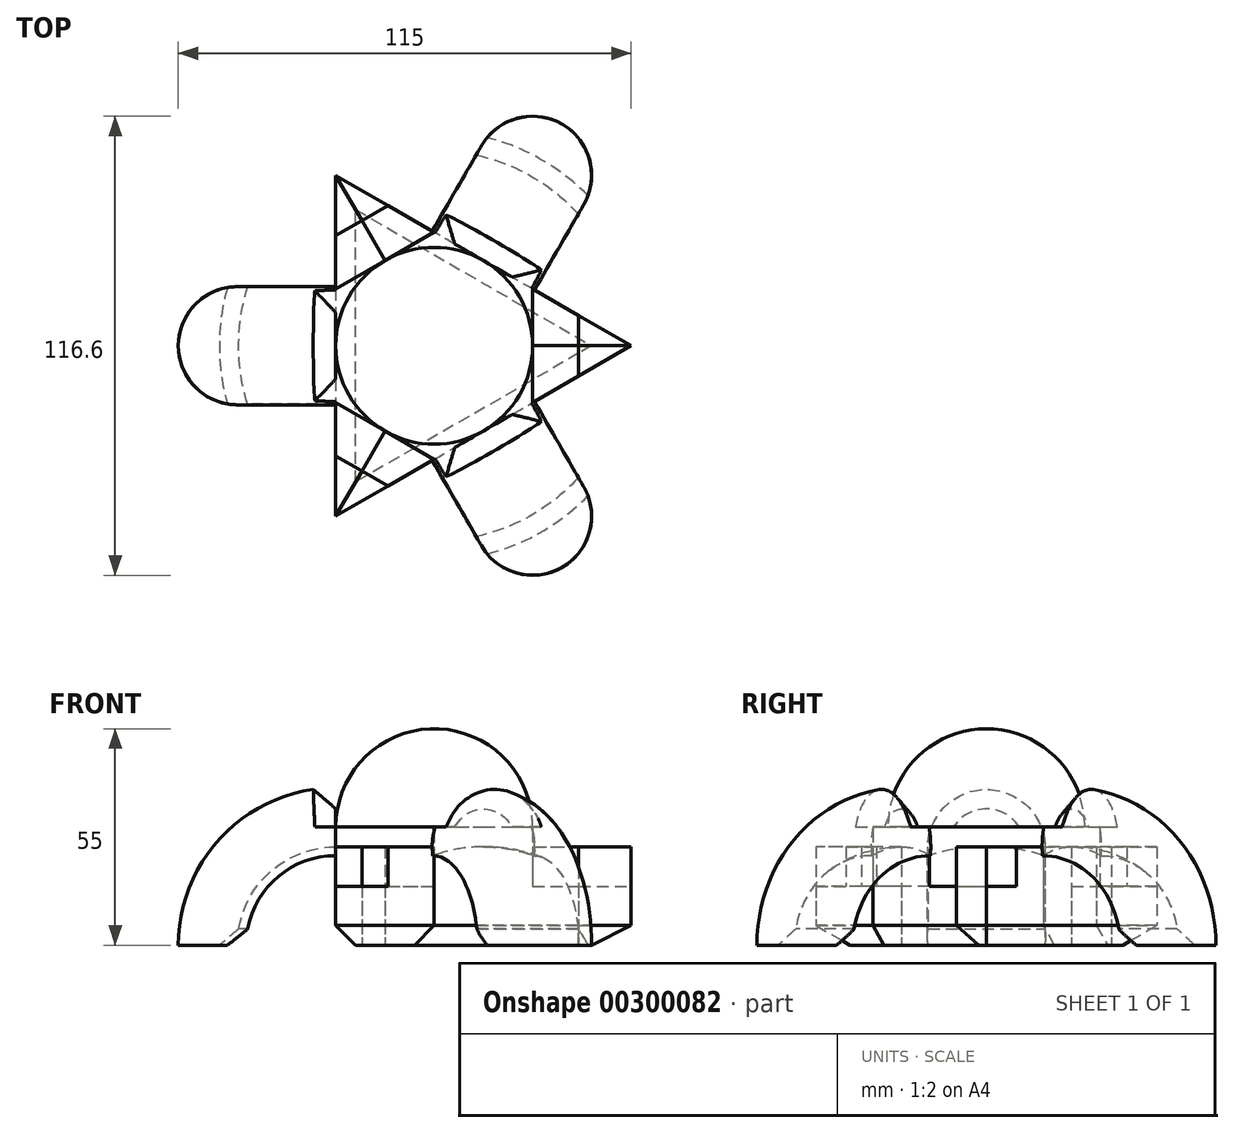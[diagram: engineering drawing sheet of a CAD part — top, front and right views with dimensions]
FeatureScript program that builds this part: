
annotation { "Feature Type Name" : "Feature", "Feature Type Description" : "" }
export const myFeature = defineFeature(function(context is Context, id is Id, definition is map)
    precondition{}
    {
        {
            var Q0;
            Q0=qCreatedBy(makeId("Top.planeOp"),FACE);
            var sketch = newSketch(context, id + "F0", { "sketchPlane" : qUnion([Q0])});
            skCircle(sketch, "E0", {"center": v(0, 0) * mm, "radius": 50 * mm});
            skCircle(sketch, "E1", {"center": v(-50, 0) * mm, "radius": 15 * mm});
            skCircle(sketch, "E2.1.0", {"center": v(25, -43.3) * mm, "radius": 15 * mm});
            skCircle(sketch, "E2.2.0", {"center": v(25, 43.3) * mm, "radius": 15 * mm});
            skLineSegment(sketch, "E3", {"start": v(-50, 0) * mm, "end": v(25, 43.3) * mm});
            skLineSegment(sketch, "E4", {"start": v(25, -43.3) * mm, "end": v(25, 43.3) * mm});
            skLineSegment(sketch, "E5", {"start": v(-50, 0) * mm, "end": v(25, -43.3) * mm});
            skLineSegment(sketch, "E6", {"start": v(25, 43.3) * mm, "end": v(-25, -43.3) * mm});
            skLineSegment(sketch, "E7", {"start": v(25, -43.3) * mm, "end": v(-25, 43.3) * mm});
            skLineSegment(sketch, "E8", {"start": v(-50, 0) * mm, "end": v(50, 0) * mm});
            skLineSegment(sketch, "E9", {"start": v(-25, 43.3) * mm, "end": v(-25, -43.3) * mm});
            skLineSegment(sketch, "E10", {"start": v(-25, 43.3) * mm, "end": v(50, 0) * mm});
            skLineSegment(sketch, "E11", {"start": v(-25, -43.3) * mm, "end": v(50, 0) * mm});
            skLineSegment(sketch, "E12", {"start": v(-47.75, -14.83) * mm, "end": v(11.03, -48.77) * mm});
            skLineSegment(sketch, "E13", {"start": v(36.72, -33.94) * mm, "end": v(36.72, 33.94) * mm});
            skLineSegment(sketch, "E14", {"start": v(11.03, 48.77) * mm, "end": v(-47.75, 14.83) * mm});
            skLineSegment(sketch, "E15", {"start": v(11.03, 48.77) * mm, "end": v(36.72, 33.94) * mm});
            skLineSegment(sketch, "E16", {"start": v(36.72, -33.94) * mm, "end": v(11.03, -48.77) * mm});
            skLineSegment(sketch, "E17", {"start": v(-47.75, -14.83) * mm, "end": v(-47.75, 14.83) * mm});
            skSolve(sketch);
        }
        {
            var Q0;
            {var subQ0=sQuery(id+"F0.wireOp",EDGE,"E11");var subQ1=sQuery(id+"F0.wireOp",EDGE,"E4");var subQ2=makeQuery(id+"F0.imprint","INTERSECT",VERTEX,{"derivedFrom":[subQ1,subQ0]});Q0=makeQuery(id+"F0.imprint","IMPRINT",FACE,{"disambiguationData":[TD([[makeQuery(id+"F0.imprint","IMPRINT",EDGE,{"disambiguationData":[TD([[subQ2,-1.0]])],"derivedFrom":subQ1}),1.0]])]});}
            var Q1;
            {var subQ0=sQuery(id+"F0.wireOp",EDGE,"E8");var subQ1=sQuery(id+"F0.wireOp",EDGE,"E4");var subQ2=makeQuery(id+"F0.imprint","INTERSECT",VERTEX,{"derivedFrom":[subQ1,subQ0]});Q1=makeQuery(id+"F0.imprint","IMPRINT",FACE,{"disambiguationData":[TD([[makeQuery(id+"F0.imprint","IMPRINT",EDGE,{"disambiguationData":[TD([[subQ2,-1.0]])],"derivedFrom":subQ1}),1.0]])]});}
            var Q2;
            {var subQ0=sQuery(id+"F0.wireOp",EDGE,"E7");var subQ1=sQuery(id+"F0.wireOp",EDGE,"E3");var subQ2=makeQuery(id+"F0.imprint","INTERSECT",VERTEX,{"derivedFrom":[subQ1,subQ0]});Q2=makeQuery(id+"F0.imprint","IMPRINT",FACE,{"disambiguationData":[TD([[makeQuery(id+"F0.imprint","IMPRINT",EDGE,{"disambiguationData":[TD([[subQ2,-1.0]])],"derivedFrom":subQ1}),-1.0]])]});}
            var Q3;
            {var subQ0=sQuery(id+"F0.wireOp",EDGE,"E9");var subQ1=sQuery(id+"F0.wireOp",EDGE,"E3");var subQ2=makeQuery(id+"F0.imprint","INTERSECT",VERTEX,{"derivedFrom":[subQ1,subQ0]});Q3=makeQuery(id+"F0.imprint","IMPRINT",FACE,{"disambiguationData":[TD([[makeQuery(id+"F0.imprint","IMPRINT",EDGE,{"disambiguationData":[TD([[subQ2,-1.0]])],"derivedFrom":subQ1}),-1.0]])]});}
            var Q4;
            {var subQ0=sQuery(id+"F0.wireOp",EDGE,"E9");var subQ1=sQuery(id+"F0.wireOp",EDGE,"E5");var subQ2=makeQuery(id+"F0.imprint","INTERSECT",VERTEX,{"derivedFrom":[subQ1,subQ0]});Q4=makeQuery(id+"F0.imprint","IMPRINT",FACE,{"disambiguationData":[TD([[makeQuery(id+"F0.imprint","IMPRINT",EDGE,{"disambiguationData":[TD([[subQ2,-1.0]])],"derivedFrom":subQ1}),1.0]])]});}
            var Q5;
            {var subQ0=sQuery(id+"F0.wireOp",EDGE,"E6");var subQ1=sQuery(id+"F0.wireOp",EDGE,"E5");var subQ2=makeQuery(id+"F0.imprint","INTERSECT",VERTEX,{"derivedFrom":[subQ1,subQ0]});Q5=makeQuery(id+"F0.imprint","IMPRINT",FACE,{"disambiguationData":[TD([[makeQuery(id+"F0.imprint","IMPRINT",EDGE,{"disambiguationData":[TD([[subQ2,-1.0]])],"derivedFrom":subQ1}),1.0]])]});}
            extrude(context, id + "F1", {"entities" : qUnion([Q0, Q1, Q2, Q3, Q4, Q5]), "depth" : 30 * mm});
        }
        {
            var Q0;
            {var subQ0=sQuery(id+"F0.wireOp",EDGE,"E0");var subQ1=makeQuery(id+"F0.imprint","INTERSECT",VERTEX,{"derivedFrom":[subQ0,sQuery(id+"F0.wireOp",EDGE,"E4"),sQuery(id+"F0.wireOp",EDGE,"E5"),sQuery(id+"F0.wireOp",EDGE,"E7")]});Q0=makeQuery(id+"F0.imprint","IMPRINT",FACE,{"disambiguationData":[TD([[makeQuery(id+"F0.imprint","IMPRINT",EDGE,{"disambiguationData":[TD([[subQ1,1.0]])],"derivedFrom":subQ0}),-1.0]])]});}
            var Q1;
            Q1=sQuery(id+"F0.wireOp",EDGE,"E11");
            revolve(context, id + "F2", {"operationType" : NewBodyOperationType.ADD, "entities" : qUnion([Q0]), "axis" : qUnion([Q1]), "revolveType" : RevolveType.ONE_DIRECTION, "oppositeDirection" : true, "angle" : 90 * degree});
        }
        {
            var Q0;
            {var subQ0=sQuery(id+"F0.wireOp",EDGE,"E0");var subQ1=makeQuery(id+"F0.imprint","INTERSECT",VERTEX,{"derivedFrom":[subQ0,sQuery(id+"F0.wireOp",EDGE,"E3"),sQuery(id+"F0.wireOp",EDGE,"E4"),sQuery(id+"F0.wireOp",EDGE,"E6")]});Q0=makeQuery(id+"F0.imprint","IMPRINT",FACE,{"disambiguationData":[TD([[makeQuery(id+"F0.imprint","IMPRINT",EDGE,{"disambiguationData":[TD([[subQ1,1.0]])],"derivedFrom":subQ0}),-1.0]])]});}
            var Q1;
            Q1=sQuery(id+"F0.wireOp",EDGE,"E10");
            revolve(context, id + "F3", {"operationType" : NewBodyOperationType.ADD, "entities" : qUnion([Q0]), "axis" : qUnion([Q1]), "revolveType" : RevolveType.ONE_DIRECTION, "angle" : 90 * degree});
        }
        {
            var Q0;
            {var subQ0=sQuery(id+"F0.wireOp",EDGE,"E0");var subQ1=makeQuery(id+"F0.imprint","INTERSECT",VERTEX,{"derivedFrom":[subQ0,sQuery(id+"F0.wireOp",EDGE,"E3"),sQuery(id+"F0.wireOp",EDGE,"E5"),sQuery(id+"F0.wireOp",EDGE,"E8")]});Q0=makeQuery(id+"F0.imprint","IMPRINT",FACE,{"disambiguationData":[TD([[makeQuery(id+"F0.imprint","IMPRINT",EDGE,{"disambiguationData":[TD([[subQ1,1.0]])],"derivedFrom":subQ0}),-1.0]])]});}
            var Q1;
            Q1=sQuery(id+"F0.wireOp",EDGE,"E9");
            revolve(context, id + "F4", {"entities" : qUnion([Q0]), "axis" : qUnion([Q1]), "revolveType" : RevolveType.ONE_DIRECTION, "oppositeDirection" : true, "angle" : 90 * degree});
        }
        {
            var Q0;
            Q0=makeQuery(id+"F4.opRevolve","SWEPT_BODY",BODY,{"disambiguationData":[OSD([sQuery(id+"F0.wireOp",EDGE,"E0"),sQuery(id+"F0.wireOp",EDGE,"E1")])]});
            deleteBodies(context, id + "F5", {"entities" : qUnion([Q0])});
        }
        {
            var Q0;
            {var subQ0=sQuery(id+"F0.wireOp",EDGE,"E0");var subQ1=makeQuery(id+"F0.imprint","INTERSECT",VERTEX,{"derivedFrom":[subQ0,sQuery(id+"F0.wireOp",EDGE,"E3"),sQuery(id+"F0.wireOp",EDGE,"E5"),sQuery(id+"F0.wireOp",EDGE,"E8")]});Q0=makeQuery(id+"F0.imprint","IMPRINT",FACE,{"disambiguationData":[TD([[makeQuery(id+"F0.imprint","IMPRINT",EDGE,{"disambiguationData":[TD([[subQ1,1.0]])],"derivedFrom":subQ0}),-1.0]])]});}
            var Q1;
            Q1=sQuery(id+"F0.wireOp",EDGE,"E9");
            revolve(context, id + "F6", {"operationType" : NewBodyOperationType.ADD, "entities" : qUnion([Q0]), "axis" : qUnion([Q1]), "revolveType" : RevolveType.ONE_DIRECTION, "oppositeDirection" : true, "angle" : 90 * degree});
        }
        {
            var Q0;
            {var subQ1=sQuery(id+"F0.wireOp",EDGE,"E6");var subQ3=sQuery(id+"F0.wireOp",EDGE,"E12");var subQ4=makeQuery(id+"F0.imprint","INTERSECT",VERTEX,{"derivedFrom":[subQ1,subQ3]});Q0=makeQuery(id+"F0.imprint","IMPRINT",FACE,{"disambiguationData":[TD([[makeQuery(id+"F0.imprint","IMPRINT",EDGE,{"disambiguationData":[TD([[subQ4,-1.0]])],"derivedFrom":subQ3}),-1.0]])]});}
            var Q1;
            {var subQ0=sQuery(id+"F0.wireOp",EDGE,"E9");var subQ1=sQuery(id+"F0.wireOp",EDGE,"E5");var subQ2=makeQuery(id+"F0.imprint","INTERSECT",VERTEX,{"derivedFrom":[subQ1,subQ0]});Q1=makeQuery(id+"F0.imprint","IMPRINT",FACE,{"disambiguationData":[TD([[makeQuery(id+"F0.imprint","IMPRINT",EDGE,{"disambiguationData":[TD([[subQ2,-1.0]])],"derivedFrom":subQ1}),-1.0]])]});}
            var Q2;
            {var subQ1=sQuery(id+"F0.wireOp",EDGE,"E7");var subQ3=sQuery(id+"F0.wireOp",EDGE,"E14");var subQ4=makeQuery(id+"F0.imprint","INTERSECT",VERTEX,{"derivedFrom":[subQ1,subQ3]});Q2=makeQuery(id+"F0.imprint","IMPRINT",FACE,{"disambiguationData":[TD([[makeQuery(id+"F0.imprint","IMPRINT",EDGE,{"disambiguationData":[TD([[subQ4,-1.0]])],"derivedFrom":subQ3}),-1.0]])]});}
            var Q3;
            {var subQ0=sQuery(id+"F0.wireOp",EDGE,"E7");var subQ1=sQuery(id+"F0.wireOp",EDGE,"E3");var subQ2=makeQuery(id+"F0.imprint","INTERSECT",VERTEX,{"derivedFrom":[subQ1,subQ0]});Q3=makeQuery(id+"F0.imprint","IMPRINT",FACE,{"disambiguationData":[TD([[makeQuery(id+"F0.imprint","IMPRINT",EDGE,{"disambiguationData":[TD([[subQ2,-1.0]])],"derivedFrom":subQ1}),1.0]])]});}
            var Q4;
            {var subQ1=sQuery(id+"F0.wireOp",EDGE,"E8");var subQ3=sQuery(id+"F0.wireOp",EDGE,"E13");var subQ4=makeQuery(id+"F0.imprint","INTERSECT",VERTEX,{"derivedFrom":[subQ1,subQ3]});Q4=makeQuery(id+"F0.imprint","IMPRINT",FACE,{"disambiguationData":[TD([[makeQuery(id+"F0.imprint","IMPRINT",EDGE,{"disambiguationData":[TD([[subQ4,-1.0]])],"derivedFrom":subQ3}),-1.0]])]});}
            var Q5;
            {var subQ0=sQuery(id+"F0.wireOp",EDGE,"E11");var subQ1=sQuery(id+"F0.wireOp",EDGE,"E4");var subQ2=makeQuery(id+"F0.imprint","INTERSECT",VERTEX,{"derivedFrom":[subQ1,subQ0]});Q5=makeQuery(id+"F0.imprint","IMPRINT",FACE,{"disambiguationData":[TD([[makeQuery(id+"F0.imprint","IMPRINT",EDGE,{"disambiguationData":[TD([[subQ2,-1.0]])],"derivedFrom":subQ1}),-1.0]])]});}
            extrude(context, id + "F7", {"entities" : qUnion([Q0, Q1, Q2, Q3, Q4, Q5]), "operationType" : NewBodyOperationType.ADD, "depth" : 15 * mm});
        }
        {
            var Q0;
            {var subQ1=sQuery(id+"F0.wireOp",EDGE,"E6");var subQ3=sQuery(id+"F0.wireOp",EDGE,"E12");var subQ4=makeQuery(id+"F0.imprint","INTERSECT",VERTEX,{"derivedFrom":[subQ1,subQ3]});Q0=makeQuery(id+"F0.imprint","IMPRINT",FACE,{"disambiguationData":[TD([[makeQuery(id+"F0.imprint","IMPRINT",EDGE,{"disambiguationData":[TD([[subQ4,1.0]])],"derivedFrom":subQ3}),-1.0]])]});}
            var Q1;
            {var subQ0=sQuery(id+"F0.wireOp",EDGE,"E6");var subQ1=sQuery(id+"F0.wireOp",EDGE,"E5");var subQ2=makeQuery(id+"F0.imprint","INTERSECT",VERTEX,{"derivedFrom":[subQ1,subQ0]});Q1=makeQuery(id+"F0.imprint","IMPRINT",FACE,{"disambiguationData":[TD([[makeQuery(id+"F0.imprint","IMPRINT",EDGE,{"disambiguationData":[TD([[subQ2,-1.0]])],"derivedFrom":subQ1}),-1.0]])]});}
            var Q2;
            {var subQ1=sQuery(id+"F0.wireOp",EDGE,"E8");var subQ3=sQuery(id+"F0.wireOp",EDGE,"E13");var subQ4=makeQuery(id+"F0.imprint","INTERSECT",VERTEX,{"derivedFrom":[subQ1,subQ3]});Q2=makeQuery(id+"F0.imprint","IMPRINT",FACE,{"disambiguationData":[TD([[makeQuery(id+"F0.imprint","IMPRINT",EDGE,{"disambiguationData":[TD([[subQ4,1.0]])],"derivedFrom":subQ3}),-1.0]])]});}
            var Q3;
            {var subQ0=sQuery(id+"F0.wireOp",EDGE,"E8");var subQ1=sQuery(id+"F0.wireOp",EDGE,"E4");var subQ2=makeQuery(id+"F0.imprint","INTERSECT",VERTEX,{"derivedFrom":[subQ1,subQ0]});Q3=makeQuery(id+"F0.imprint","IMPRINT",FACE,{"disambiguationData":[TD([[makeQuery(id+"F0.imprint","IMPRINT",EDGE,{"disambiguationData":[TD([[subQ2,-1.0]])],"derivedFrom":subQ1}),-1.0]])]});}
            var Q4;
            {var subQ0=sQuery(id+"F0.wireOp",EDGE,"E9");var subQ1=sQuery(id+"F0.wireOp",EDGE,"E3");var subQ2=makeQuery(id+"F0.imprint","INTERSECT",VERTEX,{"derivedFrom":[subQ1,subQ0]});Q4=makeQuery(id+"F0.imprint","IMPRINT",FACE,{"disambiguationData":[TD([[makeQuery(id+"F0.imprint","IMPRINT",EDGE,{"disambiguationData":[TD([[subQ2,-1.0]])],"derivedFrom":subQ1}),1.0]])]});}
            var Q5;
            {var subQ1=sQuery(id+"F0.wireOp",EDGE,"E7");var subQ3=sQuery(id+"F0.wireOp",EDGE,"E14");var subQ4=makeQuery(id+"F0.imprint","INTERSECT",VERTEX,{"derivedFrom":[subQ1,subQ3]});Q5=makeQuery(id+"F0.imprint","IMPRINT",FACE,{"disambiguationData":[TD([[makeQuery(id+"F0.imprint","IMPRINT",EDGE,{"disambiguationData":[TD([[subQ4,1.0]])],"derivedFrom":subQ3}),-1.0]])]});}
            extrude(context, id + "F8", {"entities" : qUnion([Q0, Q1, Q2, Q3, Q4, Q5]), "depth" : 25 * mm});
        }
        {
            var Q0;
            Q0=makeQuery(id+"F1.opExtrude","CAP_FACE",FACE,{"disambiguationData":[OSD([sQuery(id+"F0.wireOp",EDGE,"E3"),sQuery(id+"F0.wireOp",EDGE,"E4"),sQuery(id+"F0.wireOp",EDGE,"E5"),sQuery(id+"F0.wireOp",EDGE,"E9"),sQuery(id+"F0.wireOp",EDGE,"E10"),sQuery(id+"F0.wireOp",EDGE,"E11")])],"isStart":false});
            cPlane(context, id + "F9", {"entities" : qUnion([Q0]), "cplaneType" : CPlaneType.OFFSET, "offset" : 0 * mm, "width" : 150 * mm, "height" : 150 * mm});
        }
        {
            var Q0;
            Q0=qCreatedBy(id+"F9.planeOp",FACE);
            var sketch = newSketch(context, id + "F10", { "sketchPlane" : qUnion([Q0])});
            skCircle(sketch, "E18", {"center": v(0, 0) * mm, "radius": 50 * mm});
            skLineSegment(sketch, "E19", {"start": v(0, 0) * mm, "end": v(50, 0) * mm});
            skLineSegment(sketch, "E20", {"start": v(0, 0) * mm, "end": v(-50, 0) * mm});
            skCircle(sketch, "E21", {"center": v(-50, 0) * mm, "radius": 15 * mm});
            skCircle(sketch, "E22.1.0", {"center": v(25, -43.3) * mm, "radius": 15 * mm});
            skCircle(sketch, "E22.2.0", {"center": v(25, 43.3) * mm, "radius": 15 * mm});
            skLineSegment(sketch, "E23", {"start": v(-50, 0) * mm, "end": v(25, 43.3) * mm});
            skLineSegment(sketch, "E24", {"start": v(25, -43.3) * mm, "end": v(25, 43.3) * mm});
            skLineSegment(sketch, "E25", {"start": v(-50, 0) * mm, "end": v(25, -43.3) * mm});
            skLineSegment(sketch, "E26", {"start": v(0, 0) * mm, "end": v(25, 43.3) * mm});
            skLineSegment(sketch, "E27", {"start": v(0, 0) * mm, "end": v(25, -43.3) * mm});
            skLineSegment(sketch, "E28", {"start": v(25, -43.3) * mm, "end": v(50, 0) * mm});
            skLineSegment(sketch, "E29", {"start": v(50, 0) * mm, "end": v(25, 43.3) * mm});
            skLineSegment(sketch, "E30", {"start": v(25, 43.3) * mm, "end": v(-25, 43.3) * mm});
            skLineSegment(sketch, "E31", {"start": v(-25, 43.3) * mm, "end": v(-50, 0) * mm});
            skLineSegment(sketch, "E32", {"start": v(-50, 0) * mm, "end": v(-25, -43.3) * mm});
            skLineSegment(sketch, "E33", {"start": v(-25, -43.3) * mm, "end": v(25, -43.3) * mm});
            skLineSegment(sketch, "E34", {"start": v(50, 0) * mm, "end": v(-25, 43.3) * mm});
            skLineSegment(sketch, "E35", {"start": v(-25, 43.3) * mm, "end": v(-25, -43.3) * mm});
            skLineSegment(sketch, "E36", {"start": v(-25, -43.3) * mm, "end": v(50, 0) * mm});
            skCircle(sketch, "E37", {"center": v(0, 0) * mm, "radius": 25 * mm});
            skLineSegment(sketch, "E38", {"start": v(0, 0) * mm, "end": v(-12.5, -21.65) * mm});
            skSolve(sketch);
        }
        {
            var Q0;
            {var subQ0=sQuery(id+"F10.wireOp",EDGE,"E38");Q0=makeQuery(id+"F10.imprint","IMPRINT",FACE,{"disambiguationData":[TD([[makeQuery(id+"F10.imprint","IMPRINT",EDGE,{"derivedFrom":subQ0}),-1.0]])]});}
            var Q1;
            {var subQ3=sQuery(id+"F10.wireOp",EDGE,"E37");var subQ6=makeQuery(id+"F10.imprint","INTERSECT",VERTEX,{"derivedFrom":[sQuery(id+"F10.wireOp",EDGE,"E23"),subQ3]});Q1=makeQuery(id+"F10.imprint","IMPRINT",FACE,{"disambiguationData":[TD([[makeQuery(id+"F10.imprint","IMPRINT",EDGE,{"disambiguationData":[TD([[subQ6,1.0]])],"derivedFrom":subQ3}),1.0]])]});}
            var Q2;
            Q2=sQuery(id+"F10.wireOp",EDGE,"E26");
            revolve(context, id + "F11", {"operationType" : NewBodyOperationType.ADD, "entities" : qUnion([Q0, Q1]), "axis" : qUnion([Q2]), "revolveType" : RevolveType.FULL});
        }
        {
            var Q0;
            {var subQ0=sQuery(id+"F0.wireOp",EDGE,"E13");var subQ1=sQuery(id+"F0.wireOp",EDGE,"E8");Q0=makeQuery(id+"F7.boolean.opBoolean","MERGE",BODY,{"derivedFrom":[makeQuery(id+"F7.opExtrude","SWEPT_BODY",BODY,{"disambiguationData":[OSD([sQuery(id+"F0.wireOp",EDGE,"E4"),subQ1,sQuery(id+"F0.wireOp",EDGE,"E11"),subQ0])]}),makeQuery(id+"F7.opExtrude","SWEPT_BODY",BODY,{"disambiguationData":[OSD([subQ1,sQuery(id+"F0.wireOp",EDGE,"E10"),subQ0])]})]});}
            var Q1;
            Q1=makeQuery(id+"F1.opExtrude","SWEPT_BODY",BODY,{"disambiguationData":[OSD([sQuery(id+"F0.wireOp",EDGE,"E3"),sQuery(id+"F0.wireOp",EDGE,"E4"),sQuery(id+"F0.wireOp",EDGE,"E5"),sQuery(id+"F0.wireOp",EDGE,"E9"),sQuery(id+"F0.wireOp",EDGE,"E10"),sQuery(id+"F0.wireOp",EDGE,"E11")])]});
            var Q2;
            {var subQ0=sQuery(id+"F0.wireOp",EDGE,"E14");var subQ1=sQuery(id+"F0.wireOp",EDGE,"E7");Q2=makeQuery(id+"F7.boolean.opBoolean","MERGE",BODY,{"derivedFrom":[makeQuery(id+"F7.opExtrude","SWEPT_BODY",BODY,{"disambiguationData":[OSD([sQuery(id+"F0.wireOp",EDGE,"E3"),subQ1,sQuery(id+"F0.wireOp",EDGE,"E10"),subQ0])]}),makeQuery(id+"F7.opExtrude","SWEPT_BODY",BODY,{"disambiguationData":[OSD([subQ1,sQuery(id+"F0.wireOp",EDGE,"E9"),subQ0])]})]});}
            var Q3;
            Q3=makeQuery(id+"F8.opExtrude","SWEPT_BODY",BODY,{"disambiguationData":[OSD([sQuery(id+"F0.wireOp",EDGE,"E4"),sQuery(id+"F0.wireOp",EDGE,"E8"),sQuery(id+"F0.wireOp",EDGE,"E10"),sQuery(id+"F0.wireOp",EDGE,"E13")])]});
            var Q4;
            Q4=makeQuery(id+"F8.opExtrude","SWEPT_BODY",BODY,{"disambiguationData":[OSD([sQuery(id+"F0.wireOp",EDGE,"E7"),sQuery(id+"F0.wireOp",EDGE,"E10"),sQuery(id+"F0.wireOp",EDGE,"E14")])]});
            booleanBodies(context, id + "F12", {"operationType" : BooleanOperationType.UNION, "tools" : qUnion([Q0, Q1, Q2, Q3, Q4])});
        }
        {
            var Q0;
            Q0=makeQuery(id+"F8.opExtrude","SWEPT_BODY",BODY,{"disambiguationData":[OSD([sQuery(id+"F0.wireOp",EDGE,"E6"),sQuery(id+"F0.wireOp",EDGE,"E9"),sQuery(id+"F0.wireOp",EDGE,"E12")])]});
            var Q1;
            {var subQ0=sQuery(id+"F0.wireOp",EDGE,"E13");var subQ1=sQuery(id+"F0.wireOp",EDGE,"E8");Q1=makeQuery(id+"F7.boolean.opBoolean","MERGE",BODY,{"derivedFrom":[makeQuery(id+"F7.opExtrude","SWEPT_BODY",BODY,{"disambiguationData":[OSD([sQuery(id+"F0.wireOp",EDGE,"E4"),subQ1,sQuery(id+"F0.wireOp",EDGE,"E11"),subQ0])]}),makeQuery(id+"F7.opExtrude","SWEPT_BODY",BODY,{"disambiguationData":[OSD([subQ1,sQuery(id+"F0.wireOp",EDGE,"E10"),subQ0])]})]});}
            booleanBodies(context, id + "F13", {"operationType" : BooleanOperationType.UNION, "tools" : qUnion([Q0, Q1])});
        }
        {
            var Q0;
            Q0=makeQuery(id+"F8.opExtrude","SWEPT_BODY",BODY,{"disambiguationData":[OSD([sQuery(id+"F0.wireOp",EDGE,"E5"),sQuery(id+"F0.wireOp",EDGE,"E6"),sQuery(id+"F0.wireOp",EDGE,"E11"),sQuery(id+"F0.wireOp",EDGE,"E12")])]});
            var Q1;
            {var subQ0=sQuery(id+"F0.wireOp",EDGE,"E12");var subQ1=sQuery(id+"F0.wireOp",EDGE,"E6");Q1=makeQuery(id+"F7.boolean.opBoolean","MERGE",BODY,{"derivedFrom":[makeQuery(id+"F7.opExtrude","SWEPT_BODY",BODY,{"disambiguationData":[OSD([sQuery(id+"F0.wireOp",EDGE,"E5"),subQ1,sQuery(id+"F0.wireOp",EDGE,"E9"),subQ0])]}),makeQuery(id+"F7.opExtrude","SWEPT_BODY",BODY,{"disambiguationData":[OSD([subQ1,sQuery(id+"F0.wireOp",EDGE,"E11"),subQ0])]})]});}
            booleanBodies(context, id + "F14", {"operationType" : BooleanOperationType.UNION, "tools" : qUnion([Q0, Q1])});
        }
        {
            var Q0;
            {var subQ0=sQuery(id+"F0.wireOp",EDGE,"E10");var subQ1=makeQuery(id+"F0.imprint","INTERSECT",VERTEX,{"derivedFrom":[subQ0,sQuery(id+"F0.wireOp",EDGE,"E13")]});var subQ3=makeQuery(id+"F0.imprint","INTERSECT",VERTEX,{"derivedFrom":[subQ0,sQuery(id+"F0.wireOp",EDGE,"E14")]});Q0=makeQuery(id+"F12.opBoolean","MERGE",EDGE,{"derivedFrom":[makeQuery(id+"F7.opExtrude","CAP_EDGE",EDGE,{"disambiguationData":[OSD([subQ0]),TDD([makeQuery(id+"F0.imprint","IMPRINT",EDGE,{"disambiguationData":[TD([[subQ1,-1.0]])],"derivedFrom":subQ0})])],"isStart":true}),makeQuery(id+"F7.boolean.opBoolean","MERGE",EDGE,{"derivedFrom":[makeQuery(id+"F1.opExtrude","CAP_EDGE",EDGE,{"disambiguationData":[OSD([subQ0])],"isStart":true}),makeQuery(id+"F7.opExtrude","CAP_EDGE",EDGE,{"disambiguationData":[OSD([subQ0]),TDD([makeQuery(id+"F0.imprint","IMPRINT",EDGE,{"disambiguationData":[TD([[makeQuery(id+"F0.imprint","INTERSECT",VERTEX,{"derivedFrom":[sQuery(id+"F0.wireOp",EDGE,"E3"),subQ0]}),1.0]])],"derivedFrom":subQ0})])],"isStart":true})]}),makeQuery(id+"F8.opExtrude","CAP_EDGE",EDGE,{"disambiguationData":[OSD([subQ0]),TDD([makeQuery(id+"F0.imprint","IMPRINT",EDGE,{"disambiguationData":[TD([[subQ3,1.0]])],"derivedFrom":subQ0})])],"isStart":true}),makeQuery(id+"F8.opExtrude","CAP_EDGE",EDGE,{"disambiguationData":[OSD([subQ0]),TDD([makeQuery(id+"F0.imprint","IMPRINT",EDGE,{"disambiguationData":[TD([[makeQuery(id+"F0.imprint","INTERSECT",VERTEX,{"derivedFrom":[sQuery(id+"F0.wireOp",EDGE,"E4"),subQ0]}),-1.0]])],"derivedFrom":subQ0})])],"isStart":true})]});}
            var Q1;
            {var subQ0=sQuery(id+"F0.wireOp",EDGE,"E11");Q1=makeQuery(id+"F7.boolean.opBoolean","MERGE",EDGE,{"derivedFrom":[makeQuery(id+"F1.opExtrude","CAP_EDGE",EDGE,{"disambiguationData":[OSD([subQ0])],"isStart":true}),makeQuery(id+"F7.opExtrude","CAP_EDGE",EDGE,{"disambiguationData":[OSD([subQ0]),TDD([makeQuery(id+"F0.imprint","IMPRINT",EDGE,{"disambiguationData":[TD([[makeQuery(id+"F0.imprint","INTERSECT",VERTEX,{"derivedFrom":[sQuery(id+"F0.wireOp",EDGE,"E4"),subQ0]}),-1.0]])],"derivedFrom":subQ0})])],"isStart":true})]});}
            var Q2;
            {var subQ0=sQuery(id+"F0.wireOp",EDGE,"E11");var subQ1=makeQuery(id+"F0.imprint","INTERSECT",VERTEX,{"derivedFrom":[subQ0,sQuery(id+"F0.wireOp",EDGE,"E12")]});Q2=makeQuery(id+"F14.opBoolean","MERGE",EDGE,{"derivedFrom":[makeQuery(id+"F7.opExtrude","CAP_EDGE",EDGE,{"disambiguationData":[OSD([subQ0]),TDD([makeQuery(id+"F0.imprint","IMPRINT",EDGE,{"disambiguationData":[TD([[subQ1,1.0]])],"derivedFrom":subQ0})])],"isStart":true}),makeQuery(id+"F8.opExtrude","CAP_EDGE",EDGE,{"disambiguationData":[OSD([subQ0]),TDD([makeQuery(id+"F0.imprint","IMPRINT",EDGE,{"disambiguationData":[TD([[makeQuery(id+"F0.imprint","INTERSECT",VERTEX,{"derivedFrom":[sQuery(id+"F0.wireOp",EDGE,"E5"),subQ0]}),1.0]])],"derivedFrom":subQ0})])],"isStart":true})]});}
            var Q3;
            {var subQ0=sQuery(id+"F0.wireOp",EDGE,"E11");Q3=makeQuery(id+"F8.opExtrude","CAP_EDGE",EDGE,{"disambiguationData":[OSD([subQ0]),TDD([makeQuery(id+"F0.imprint","IMPRINT",EDGE,{"disambiguationData":[TD([[makeQuery(id+"F0.imprint","INTERSECT",VERTEX,{"derivedFrom":[subQ0,sQuery(id+"F0.wireOp",EDGE,"E13")]}),-1.0]])],"derivedFrom":subQ0})])],"isStart":true});}
            var Q4;
            {var subQ0=sQuery(id+"F0.wireOp",EDGE,"E9");var subQ1=makeQuery(id+"F0.imprint","INTERSECT",VERTEX,{"derivedFrom":[subQ0,sQuery(id+"F0.wireOp",EDGE,"E12")]});Q4=makeQuery(id+"F13.opBoolean","MERGE",EDGE,{"derivedFrom":[makeQuery(id+"F7.boolean.opBoolean","MERGE",EDGE,{"derivedFrom":[makeQuery(id+"F1.opExtrude","CAP_EDGE",EDGE,{"disambiguationData":[OSD([subQ0])],"isStart":true}),makeQuery(id+"F7.opExtrude","CAP_EDGE",EDGE,{"disambiguationData":[OSD([subQ0]),TDD([makeQuery(id+"F0.imprint","IMPRINT",EDGE,{"disambiguationData":[TD([[makeQuery(id+"F0.imprint","INTERSECT",VERTEX,{"derivedFrom":[sQuery(id+"F0.wireOp",EDGE,"E5"),subQ0]}),-1.0]])],"derivedFrom":subQ0})])],"isStart":true})]}),makeQuery(id+"F8.opExtrude","CAP_EDGE",EDGE,{"disambiguationData":[OSD([subQ0]),TDD([makeQuery(id+"F0.imprint","IMPRINT",EDGE,{"disambiguationData":[TD([[subQ1,-1.0]])],"derivedFrom":subQ0})])],"isStart":true})]});}
            var Q5;
            {var subQ0=sQuery(id+"F0.wireOp",EDGE,"E9");Q5=makeQuery(id+"F7.opExtrude","CAP_EDGE",EDGE,{"disambiguationData":[OSD([subQ0]),TDD([makeQuery(id+"F0.imprint","IMPRINT",EDGE,{"disambiguationData":[TD([[makeQuery(id+"F0.imprint","INTERSECT",VERTEX,{"derivedFrom":[subQ0,sQuery(id+"F0.wireOp",EDGE,"E14")]}),1.0]])],"derivedFrom":subQ0})])],"isStart":true});}
            var Q6;
            {var subQ0=sQuery(id+"F0.wireOp",EDGE,"E9");Q6=makeQuery(id+"F8.opExtrude","CAP_EDGE",EDGE,{"disambiguationData":[OSD([subQ0]),TDD([makeQuery(id+"F0.imprint","IMPRINT",EDGE,{"disambiguationData":[TD([[makeQuery(id+"F0.imprint","INTERSECT",VERTEX,{"derivedFrom":[sQuery(id+"F0.wireOp",EDGE,"E3"),subQ0]}),1.0]])],"derivedFrom":subQ0})])],"isStart":true});}
            var Q7;
            Q7=makeQuery(id+"F3.opRevolve","CAP_EDGE",EDGE,{"disambiguationData":[OSD([sQuery(id+"F0.wireOp",EDGE,"E0")])],"isStart":true});
            var Q8;
            Q8=makeQuery(id+"F6.opRevolve","CAP_EDGE",EDGE,{"disambiguationData":[OSD([sQuery(id+"F0.wireOp",EDGE,"E0")])],"isStart":true});
            var Q9;
            Q9=makeQuery(id+"F2.opRevolve","CAP_EDGE",EDGE,{"disambiguationData":[OSD([sQuery(id+"F0.wireOp",EDGE,"E0")])],"isStart":true});
            chamfer(context, id + "F15", {"entities" : qUnion([Q0, Q1, Q2, Q3, Q4, Q5, Q6, Q7, Q8, Q9]), "width" : 5 * mm, "tangentPropagation" : true});
        }
        {
            var Q0;
            {var subQ0=sQuery(id+"F0.wireOp",EDGE,"E11");var subQ1=sQuery(id+"F0.wireOp",EDGE,"E2.1.0");var subQ2=makeQuery(id+"F2.opRevolve","CAP_FACE",FACE,{"disambiguationData":[OSD([sQuery(id+"F0.wireOp",EDGE,"E0"),subQ1])],"isStart":false});var subQ3=makeQuery(id+"F2.opRevolve","SWEPT_FACE",FACE,{"disambiguationData":[OSD([subQ1])]});Q0=makeQuery(id+"F2.boolean.opBoolean","SPLIT",EDGE,{"disambiguationData":[topologyDisambiguationEdgeConnected([subQ2,subQ3]),TD([makeQuery(id+"F1.opExtrude","CAP_FACE",FACE,{"disambiguationData":[OSD([sQuery(id+"F0.wireOp",EDGE,"E3"),sQuery(id+"F0.wireOp",EDGE,"E4"),sQuery(id+"F0.wireOp",EDGE,"E5"),sQuery(id+"F0.wireOp",EDGE,"E9"),sQuery(id+"F0.wireOp",EDGE,"E10"),subQ0])],"isStart":false})])],"derivedFrom":makeQuery(id+"F2.opRevolve","CAP_EDGE",EDGE,{"disambiguationData":[OSD([subQ1])],"isStart":false})});}
            var Q1;
            {var subQ0=sQuery(id+"F0.wireOp",EDGE,"E10");var subQ1=sQuery(id+"F0.wireOp",EDGE,"E2.2.0");var subQ2=makeQuery(id+"F3.opRevolve","SWEPT_FACE",FACE,{"disambiguationData":[OSD([subQ1])]});var subQ3=makeQuery(id+"F3.opRevolve","CAP_FACE",FACE,{"disambiguationData":[OSD([sQuery(id+"F0.wireOp",EDGE,"E0"),subQ1])],"isStart":false});Q1=makeQuery(id+"F3.boolean.opBoolean","SPLIT",EDGE,{"disambiguationData":[topologyDisambiguationEdgeConnected([subQ3,subQ2]),TD([makeQuery(id+"F1.opExtrude","CAP_FACE",FACE,{"disambiguationData":[OSD([sQuery(id+"F0.wireOp",EDGE,"E3"),sQuery(id+"F0.wireOp",EDGE,"E4"),sQuery(id+"F0.wireOp",EDGE,"E5"),sQuery(id+"F0.wireOp",EDGE,"E9"),subQ0,sQuery(id+"F0.wireOp",EDGE,"E11")])],"isStart":false})])],"derivedFrom":makeQuery(id+"F3.opRevolve","CAP_EDGE",EDGE,{"disambiguationData":[OSD([subQ1])],"isStart":false})});}
            var Q2;
            {var subQ0=sQuery(id+"F0.wireOp",EDGE,"E9");var subQ1=sQuery(id+"F0.wireOp",EDGE,"E1");var subQ2=makeQuery(id+"F6.opRevolve","SWEPT_FACE",FACE,{"disambiguationData":[OSD([subQ1])]});var subQ3=makeQuery(id+"F6.opRevolve","CAP_FACE",FACE,{"disambiguationData":[OSD([sQuery(id+"F0.wireOp",EDGE,"E0"),subQ1])],"isStart":false});Q2=makeQuery(id+"F6.boolean.opBoolean","SPLIT",EDGE,{"disambiguationData":[topologyDisambiguationEdgeConnected([subQ3,subQ2]),TD([makeQuery(id+"F1.opExtrude","CAP_FACE",FACE,{"disambiguationData":[OSD([sQuery(id+"F0.wireOp",EDGE,"E3"),sQuery(id+"F0.wireOp",EDGE,"E4"),sQuery(id+"F0.wireOp",EDGE,"E5"),subQ0,sQuery(id+"F0.wireOp",EDGE,"E10"),sQuery(id+"F0.wireOp",EDGE,"E11")])],"isStart":false})])],"derivedFrom":makeQuery(id+"F6.opRevolve","CAP_EDGE",EDGE,{"disambiguationData":[OSD([subQ1])],"isStart":false})});}
            chamfer(context, id + "F16", {"entities" : qUnion([Q0, Q1, Q2]), "width" : 5 * mm, "tangentPropagation" : true});
        }
    });
